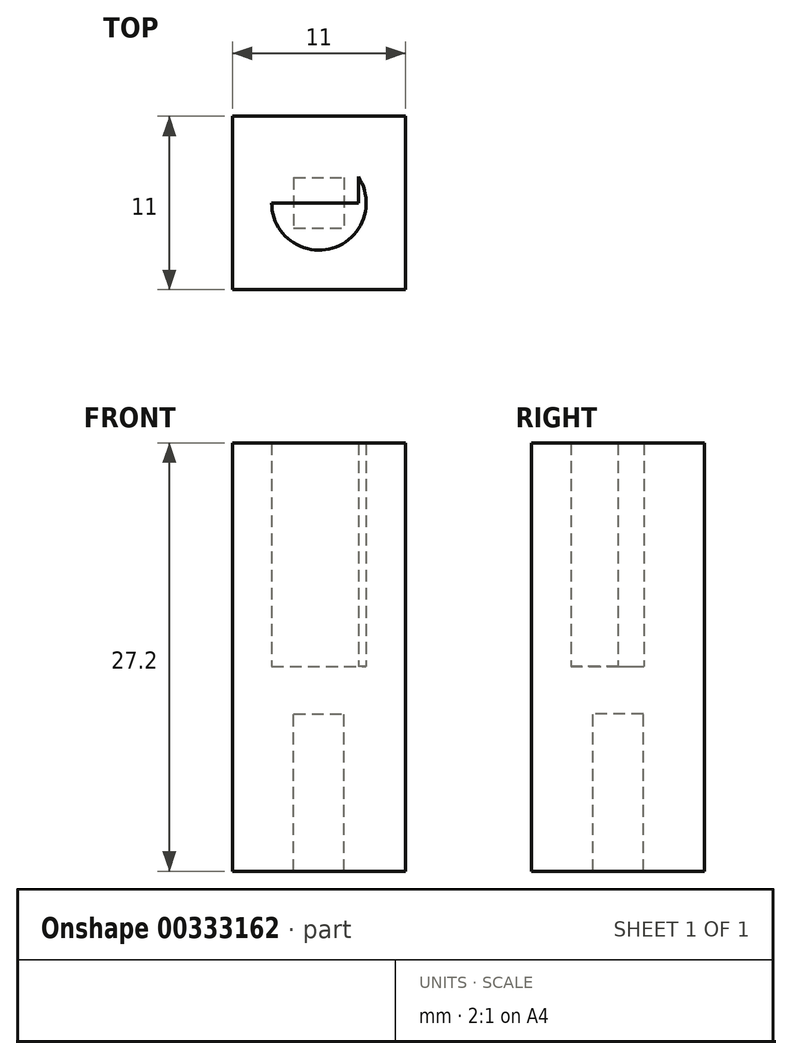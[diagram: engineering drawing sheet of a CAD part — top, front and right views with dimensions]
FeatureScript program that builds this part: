
annotation { "Feature Type Name" : "Feature", "Feature Type Description" : "" }
export const myFeature = defineFeature(function(context is Context, id is Id, definition is map)
    precondition{}
    {
        {
            var Q0;
            Q0=qCreatedBy(makeId("Top.planeOp"),FACE);
            var sketch = newSketch(context, id + "F0", { "sketchPlane" : qUnion([Q0])});
            skCircle(sketch, "E0", {"center": v(0, 0) * mm, "radius": 3 * mm});
            skLineSegment(sketch, "E1", {"start": v(-3, 0) * mm, "end": v(2.5, 0) * mm});
            skLineSegment(sketch, "E2", {"start": v(2.5, -1.66) * mm, "end": v(2.5, 1.66) * mm});
            skLineSegment(sketch, "E3.bottom", {"start": v(5.5, 5.5) * mm, "end": v(-5.5, 5.5) * mm});
            skLineSegment(sketch, "E3.top", {"start": v(5.5, -5.5) * mm, "end": v(-5.5, -5.5) * mm});
            skLineSegment(sketch, "E3.left", {"start": v(5.5, 5.5) * mm, "end": v(5.5, -5.5) * mm});
            skLineSegment(sketch, "E3.right", {"start": v(-5.5, 5.5) * mm, "end": v(-5.5, -5.5) * mm});
            skSolve(sketch);
        }
        {
            var Q0;
            Q0=makeQuery(id+"F0.imprint","IMPRINT",FACE,{"disambiguationData":[TD([[makeQuery(id+"F0.imprint","IMPRINT",EDGE,{"derivedFrom":sQuery(id+"F0.wireOp",EDGE,"ZaWfL3dz-teJq-2qJw-Bn2j-wU9BD7OHoSHv")}),1.0]])]});
            var Q1;
            {var subQ0=sQuery(id+"F0.wireOp",EDGE,"E2");var subQ1=sQuery(id+"F0.wireOp",EDGE,"E0");var subQ2=makeQuery(id+"F0.imprint","INTERSECT",VERTEX,{"disambiguationData":[OD(0.0)],"derivedFrom":[subQ1,subQ0]});Q1=makeQuery(id+"F0.imprint","IMPRINT",FACE,{"disambiguationData":[TD([[makeQuery(id+"F0.imprint","IMPRINT",EDGE,{"disambiguationData":[TD([[subQ2,-1.0]])],"derivedFrom":subQ1}),1.0]])]});}
            var Q2;
            Q2=makeQuery(id+"F0.imprint","IMPRINT",FACE,{"disambiguationData":[TD([[makeQuery(id+"F0.imprint","IMPRINT",EDGE,{"derivedFrom":sQuery(id+"F0.wireOp",EDGE,"E3.bottom")}),1.0]])]});
            extrude(context, id + "F1", {"entities" : qUnion([Q0, Q1, Q2]), "depth" : 14.2 * mm});
        }
        {
            var Q0;
            Q0=makeQuery(id+"F1.opExtrude","CAP_FACE",FACE,{"disambiguationData":[OSD([sQuery(id+"F0.wireOp",EDGE,"E0"),sQuery(id+"F0.wireOp",EDGE,"E2"),sQuery(id+"F0.wireOp",EDGE,"ZaWfL3dz-teJq-2qJw-Bn2j-wU9BD7OHoSHv")])],"isStart":true});
            var sketch = newSketch(context, id + "F2", { "sketchPlane" : qUnion([Q0])});
            skLineSegment(sketch, "E4.bottom", {"start": v(5.5, -5.5) * mm, "end": v(-5.5, -5.5) * mm});
            skLineSegment(sketch, "E4.top", {"start": v(5.5, 5.5) * mm, "end": v(-5.5, 5.5) * mm});
            skLineSegment(sketch, "E4.left", {"start": v(5.5, -5.5) * mm, "end": v(5.5, 5.5) * mm});
            skLineSegment(sketch, "E4.right", {"start": v(-5.5, -5.5) * mm, "end": v(-5.5, 5.5) * mm});
            skPoint(sketch, "E4.middle", {"position": v(0, 0) * mm});
            skSolve(sketch);
        }
        {
            var Q0;
            Q0=makeQuery(id+"F2.imprint","IMPRINT",FACE,{"disambiguationData":[TD([[makeQuery(id+"F2.imprint","IMPRINT",EDGE,{"derivedFrom":sQuery(id+"F2.wireOp",EDGE,"vzzhTCoM-K7Zn-38xK-Sv41-PlzZ2GA9Vn8e")}),-1.0]])]});
            var Q1;
            Q1=makeQuery(id+"F2.imprint","IMPRINT",FACE,{"disambiguationData":[TD([[makeQuery(id+"F2.imprint","IMPRINT",EDGE,{"derivedFrom":sQuery(id+"F2.wireOp",EDGE,"vzzhTCoM-K7Zn-38xK-Sv41-PlzZ2GA9Vn8e")}),1.0]])]});
            var Q2;
            Q2=makeQuery(id+"F2.imprint","IMPRINT",FACE,{"disambiguationData":[TD([[makeQuery(id+"F2.imprint","IMPRINT",EDGE,{"derivedFrom":makeQuery(id+"F1.opExtrude","CAP_EDGE",EDGE,{"disambiguationData":[OSD([sQuery(id+"F0.wireOp",EDGE,"E0")])],"isStart":true})}),-1.0]])]});
            var Q3;
            Q3=makeQuery(id+"F2.imprint","IMPRINT",FACE,{"disambiguationData":[TD([[makeQuery(id+"F2.imprint","IMPRINT",EDGE,{"derivedFrom":sQuery(id+"F2.wireOp",EDGE,"E4.bottom")}),-1.0]])]});
            extrude(context, id + "F3", {"entities" : qUnion([Q0, Q1, Q2, Q3]), "operationType" : NewBodyOperationType.ADD, "depth" : 3 * mm});
        }
        {
            var Q0;
            Q0=makeQuery(id+"F3.opExtrude","CAP_FACE",FACE,{"disambiguationData":[OSD([sQuery(id+"F2.wireOp",EDGE,"E4.bottom"),sQuery(id+"F2.wireOp",EDGE,"E4.top"),sQuery(id+"F2.wireOp",EDGE,"E4.left"),sQuery(id+"F2.wireOp",EDGE,"E4.right")])],"isStart":false});
            var sketch = newSketch(context, id + "F4", { "sketchPlane" : qUnion([Q0])});
            skLineSegment(sketch, "E5.bottom", {"start": v(-1.6, -1.6) * mm, "end": v(1.6, -1.6) * mm});
            skLineSegment(sketch, "E5.top", {"start": v(-1.6, 1.6) * mm, "end": v(1.6, 1.6) * mm});
            skLineSegment(sketch, "E5.left", {"start": v(-1.6, -1.6) * mm, "end": v(-1.6, 1.6) * mm});
            skLineSegment(sketch, "E5.right", {"start": v(1.6, -1.6) * mm, "end": v(1.6, 1.6) * mm});
            skPoint(sketch, "E5.middle", {"position": v(0, 0) * mm});
            skSolve(sketch);
        }
        {
            var Q0;
            Q0=makeQuery(id+"F4.imprint","IMPRINT",FACE,{"disambiguationData":[TD([[makeQuery(id+"F4.imprint","IMPRINT",EDGE,{"derivedFrom":sQuery(id+"F4.wireOp",EDGE,"E5.bottom")}),-1.0]])]});
            extrude(context, id + "F5", {"entities" : qUnion([Q0]), "operationType" : NewBodyOperationType.ADD, "depth" : 10 * mm});
        }
    });
